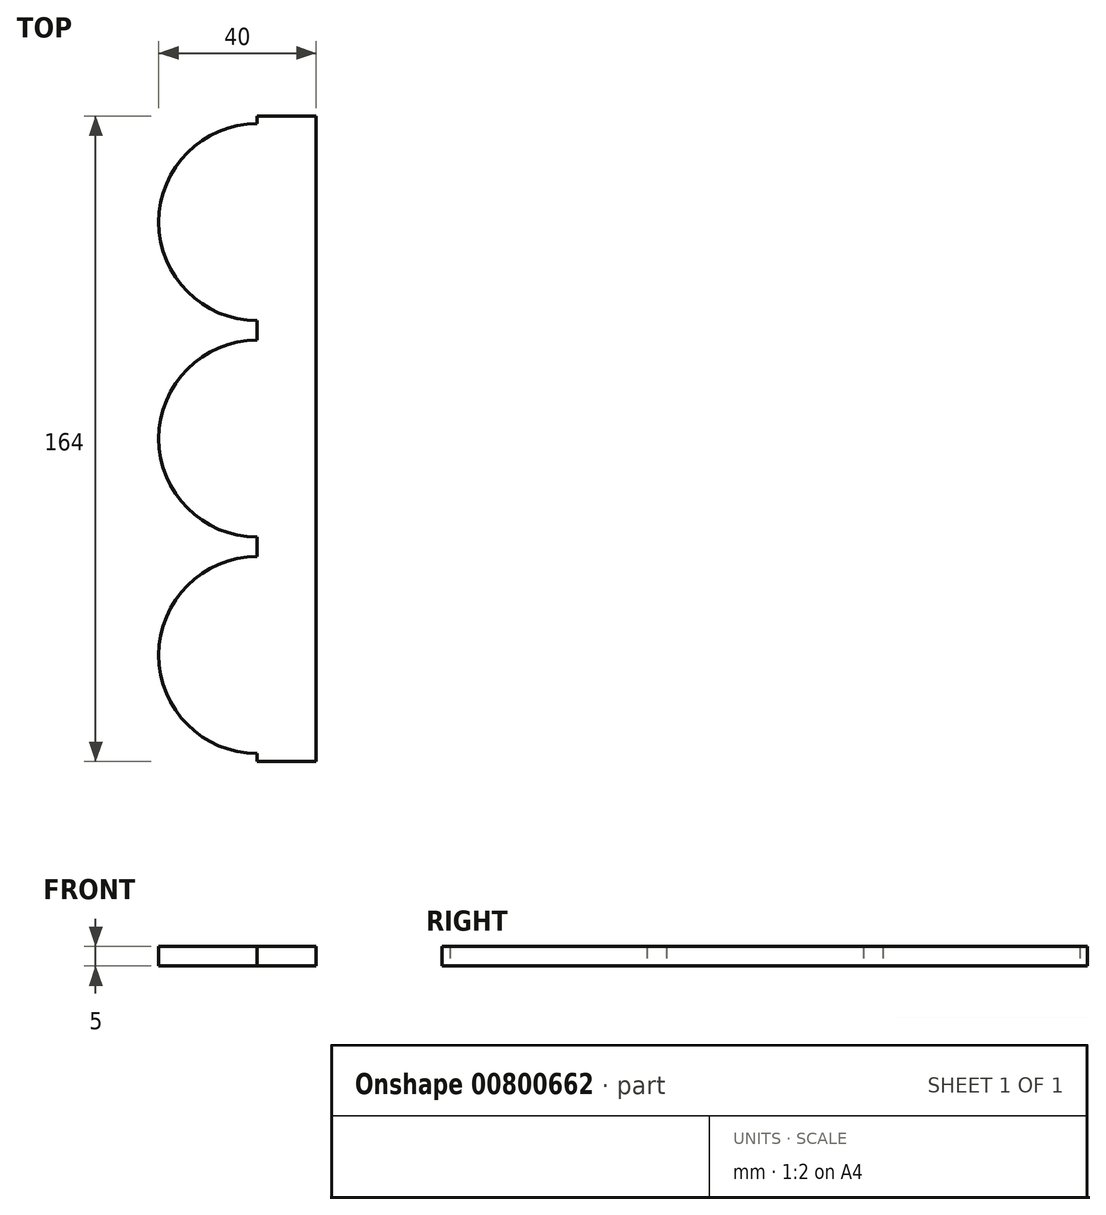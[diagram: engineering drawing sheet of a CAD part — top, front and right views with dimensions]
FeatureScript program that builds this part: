
annotation { "Feature Type Name" : "Feature", "Feature Type Description" : "" }
export const myFeature = defineFeature(function(context is Context, id is Id, definition is map)
    precondition{}
    {
        {
            var Q0;
            Q0=qCreatedBy(makeId("Top.planeOp"),FACE);
            var sketch = newSketch(context, id + "F0", { "sketchPlane" : qUnion([Q0])});
            skArc(sketch, "E0", {"start": v(0, 80) * mm, "mid": v(-25, 55) * mm, "end": v(0, 30) * mm});
            skArc(sketch, "E1", {"start": v(0, 25) * mm, "mid": v(-25, 0) * mm, "end": v(0, -25) * mm});
            skArc(sketch, "E2", {"start": v(0, -30) * mm, "mid": v(-25, -55) * mm, "end": v(0, -80) * mm});
            skLineSegment(sketch, "E3", {"start": v(0, -82) * mm, "end": v(0, -80) * mm});
            skLineSegment(sketch, "E4", {"start": v(15, 82) * mm, "end": v(15, -82) * mm});
            skLineSegment(sketch, "E5", {"start": v(15, -82) * mm, "end": v(0, -82) * mm});
            skLineSegment(sketch, "E6", {"start": v(0, 82) * mm, "end": v(15, 82) * mm});
            skLineSegment(sketch, "E7.trimOffspring", {"start": v(0, 80) * mm, "end": v(0, 82) * mm});
            skLineSegment(sketch, "E8.trimOffspring", {"start": v(0, 25) * mm, "end": v(0, 30) * mm});
            skLineSegment(sketch, "E9.trimOffspring", {"start": v(0, -30) * mm, "end": v(0, 0) * mm});
            skSolve(sketch);
        }
        {
            var Q0;
            Q0=makeQuery(id+"F0.imprint","IMPRINT",FACE,{"disambiguationData":[TD([[makeQuery(id+"F0.imprint","IMPRINT",EDGE,{"derivedFrom":sQuery(id+"F0.wireOp",EDGE,"E0")}),1.0]])]});
            extrude(context, id + "F1", {"entities" : qUnion([Q0]), "depth" : 5 * mm, "offsetDistance" : 25 * mm});
        }
    });
